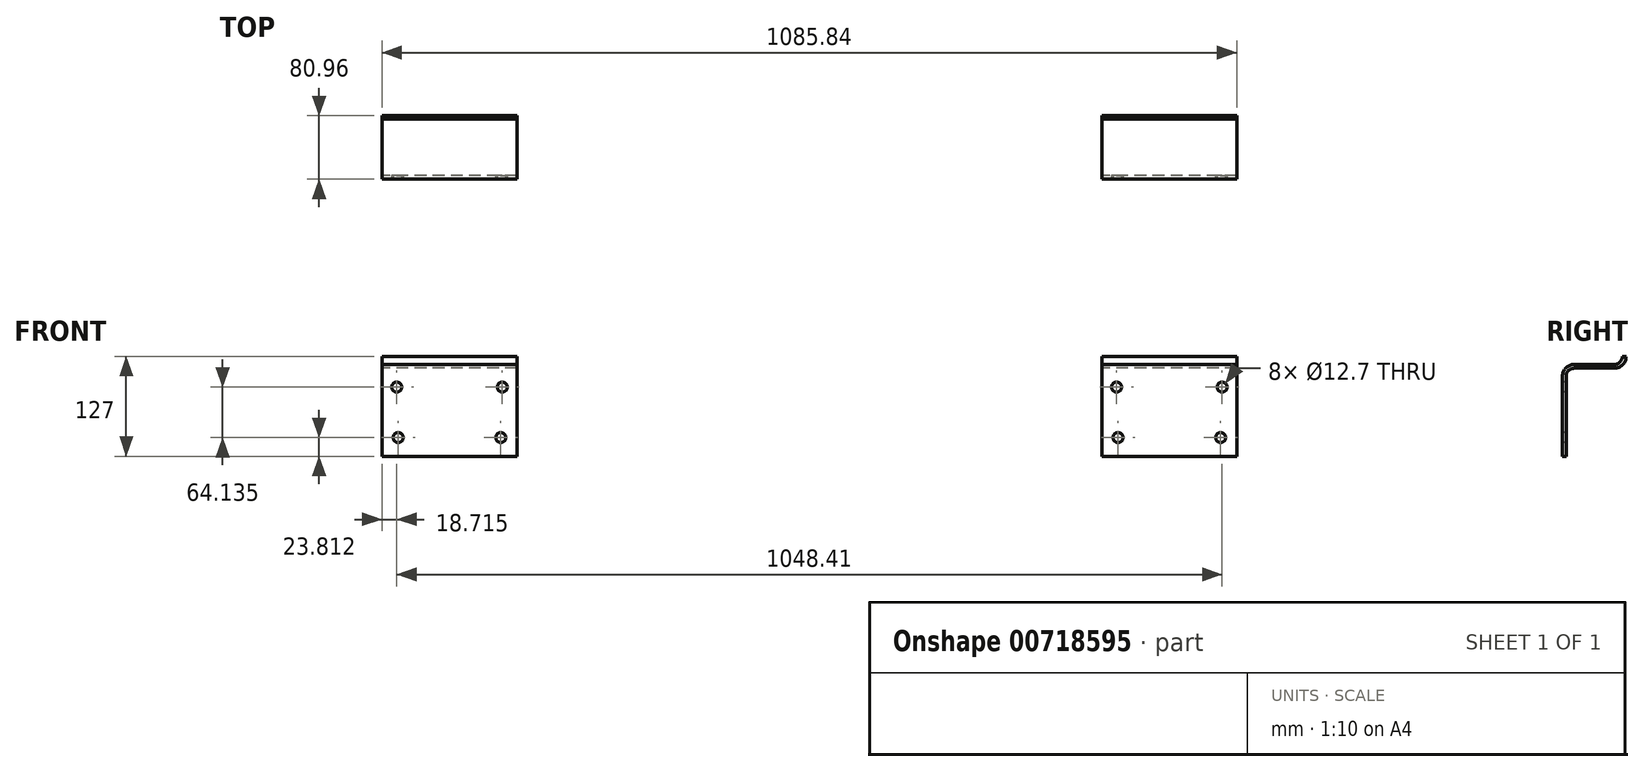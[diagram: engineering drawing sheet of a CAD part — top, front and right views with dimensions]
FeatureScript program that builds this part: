
annotation { "Feature Type Name" : "Feature", "Feature Type Description" : "" }
export const myFeature = defineFeature(function(context is Context, id is Id, definition is map)
    precondition{}
    {
        {
            var Q0;
            Q0=qCreatedBy(makeId("Right.planeOp"),FACE);
            var sketch = newSketch(context, id + "F0", { "sketchPlane" : qUnion([Q0])});
            skArc(sketch, "E0.MirrorCS", {"start": v(0, 101.6) * mm, "mid": v(3.72, 110.58) * mm, "end": v(12.7, 114.3) * mm});
            skArc(sketch, "E1.MirrorCS", {"start": v(63.5, 114.3) * mm, "mid": v(72.48, 118.02) * mm, "end": v(76.2, 127) * mm});
            skLineSegment(sketch, "E2.MirrorCS", {"start": v(12.7, 114.3) * mm, "end": v(63.5, 114.3) * mm});
            skLineSegment(sketch, "E3.MirrorCS", {"start": v(0, 0) * mm, "end": v(0, 101.6) * mm});
            skSolve(sketch);
        }
        {
            var Q0;
            Q0=qCreatedBy(makeId("Top.planeOp"),FACE);
            var sketch = newSketch(context, id + "F1", { "sketchPlane" : qUnion([Q0])});
            skLineSegment(sketch, "E4.bottom", {"start": v(85.73, 2.38) * mm, "end": v(-85.73, 2.38) * mm});
            skLineSegment(sketch, "E4.top", {"start": v(85.72, -2.38) * mm, "end": v(-85.72, -2.38) * mm});
            skLineSegment(sketch, "E4.left", {"start": v(85.73, 2.38) * mm, "end": v(85.73, -2.38) * mm});
            skLineSegment(sketch, "E4.right", {"start": v(-85.73, 2.38) * mm, "end": v(-85.73, -2.38) * mm});
            skPoint(sketch, "E4.middle", {"position": v(0, 0) * mm});
            skSolve(sketch);
        }
        {
            var Q0;
            Q0=qSketchRegion(id+"F1",true);
            var Q1;
            Q1=qSketchRegion(id+"F0",true);
            var Q2;
            Q2=qConstructionFilter(qBodyType(qCreatedBy(id+"F0",EDGE),BodyType.WIRE),ConstructionObject.NO);
            sweep(context, id + "F2", {"profiles" : qUnion([Q0, Q1]), "path" : qUnion([Q2])});
        }
        {
            var Q0;
            Q0=makeQuery(id+"F2.opSweep","SWEPT_FACE",FACE,{"disambiguationData":[OSD([sQuery(id+"F0.wireOp",EDGE,"E3.MirrorCS"),sQuery(id+"F1.wireOp",EDGE,"E4.top")])]});
            var sketch = newSketch(context, id + "F3", { "sketchPlane" : qUnion([Q0])});
            skCircle(sketch, "E5", {"center": v(-67, 87.95) * mm, "radius": 6.35 * mm});
            skCircle(sketch, "E6", {"center": v(67, 87.95) * mm, "radius": 6.35 * mm});
            skCircle(sketch, "E7", {"center": v(-65.14, 23.81) * mm, "radius": 6.35 * mm});
            skCircle(sketch, "E8", {"center": v(65.14, 23.81) * mm, "radius": 6.35 * mm});
            skLineSegment(sketch, "E9", {"start": v(0, 107) * mm, "end": v(0, 1.95) * mm, "construction": true});
            skLineSegment(sketch, "E10", {"start": v(-67, 87.95) * mm, "end": v(0, 87.95) * mm, "construction": true});
            skLineSegment(sketch, "E11", {"start": v(67, 87.95) * mm, "end": v(0, 87.95) * mm, "construction": true});
            skLineSegment(sketch, "E12", {"start": v(-65.14, 23.81) * mm, "end": v(0, 23.81) * mm, "construction": true});
            skLineSegment(sketch, "E13", {"start": v(0, 23.81) * mm, "end": v(65.14, 23.81) * mm, "construction": true});
            skSolve(sketch);
        }
        {
            var Q0;
            Q0=qSketchRegion(id+"F3",true);
            extrude(context, id + "F4", {"entities" : qUnion([Q0]), "operationType" : NewBodyOperationType.REMOVE, "endBound" : BoundingType.THROUGH_ALL, "oppositeDirection" : true, "depth" : 25.4 * mm, "offsetDistance" : 25.4 * mm});
        }
        {
            var Q0;
            Q0=makeQuery(id+"F2.opSweep","SWEPT_BODY",BODY,{"disambiguationData":[OSD([sQuery(id+"F0.wireOp",EDGE,"E3.MirrorCS"),sQuery(id+"F1.wireOp",EDGE,"E4.bottom"),sQuery(id+"F1.wireOp",EDGE,"E4.top"),sQuery(id+"F1.wireOp",EDGE,"E4.left"),sQuery(id+"F1.wireOp",EDGE,"E4.right")])]});
            var Q1;
            Q1=qCreatedBy(makeId("Right.planeOp"),FACE);
            transform(context, id + "F5", {"entities" : qUnion([Q0]), "transformType" : TransformType.TRANSLATION_DISTANCE, "transformDirection" : qUnion([Q1]), "distance" : 914.4 * mm, "makeCopy" : true});
        }
    });
